# Revit family: 0030453
name_source: partatom
category: Lighting Fixtures
revit_build: Autodesk Revit 2017 (Build: 20190507_1515(x64)
units: mm (PartAtom-declared; Revit-internal decimal feet)

## family parameters
Cut with Voids When Loaded = No
Host = Face
Light Source = Yes
OmniClass Number = 23.80.70.00
OmniClass Title = Lighting
Part Type = Normal
Room Calculation Point = No
Round Connector Dimension = Use Diameter
Shared = No

## types (8) — shared parameters
Apparent Load = 17 VA
Assembly Code = D5020200
AssetType = Fixed
ClassificationName = Uniclass2015
ClassificationValue = EF_70_80
Color Filter = 16777215
Default Elevation = 1219 mm
DiameterRecess_SYL = 200 mm  [stored 0.656168 ft]
DiameterTopBase_SYL = 200 mm  [stored 0.656168 ft]
DiameterTop_SYL = 135 mm  [stored 0.442913 ft]
Diameter_SYL = 220 mm  [stored 0.721785 ft]
Dimming Lamp Color Temperature Shift = <None>
DocumentationLiterature = http://www.sylvania-lighting.com
DurationUnit = hours
ElectricShockClassification = Class II
Emit Shape Visible in Rendering = No
Emit from Circle Diameter = 180 mm  [stored 0.590551 ft]
ExpectedLife = 50000
HeightBezel_SYL = 3 mm  [stored 0.00984252 ft]
Height_SYL = 61 mm  [stored 0.200131 ft]
IfcExportAs = IfcLightFixtureType
IfcExportType = IfcLightFixtureType
ImpactProtectionIndex = IK07
IngressProtection = IP44/20
Keynote = 16500
Lamp = LED
LampColourRenderingIndex = 80
LampColourTemperature = 4000 K
LampMacAdamStep = 3
LampNominalLuminous = 2000 lm
LampsType = LED
LuminousEfficacy = 121 lm/W
Manufacturer = Feilo Sylvania
ManufacturerName = Feilo Sylvania
Material = aluminium housing
Material_1_FEILO = Trim-Sylvania-STARTDownlight-White
Material_2_FEILO = Diffuser-Sylvania-STARTDownlight
Material_3_FEILO = Top-Sylvania-STARTDownlight
Material_4_FEILO = LED-Sylvania-STARTDownlight
Model = Insaver Slim IP44 Multipower U19 205 650-2000lm840
ModelNumber = 0030453
ModelReference = Insaver Slim IP44 Multipower U19 205 650-2000lm840
Name = Insaver Slim IP44 Multipower U19 205 650-2000lm840
NominalDepth = 220 mm  [stored 0.721785 ft]
NominalHeight = 60 mm  [stored 0.19685 ft]
NominalLength = 220 mm  [stored 0.721785 ft]
PowerConsumption = 16.5 W
PowerFactor = 0.9
RadiusReflector_SYL = 100 mm  [stored 0.328084 ft]
RadiusTop_SYL = 6 mm  [stored 0.019685 ft]
Size1_SYL = No
Size2_SYL = No
Size3PIR_SYL = No
Size4_SYL = Yes
Tilt Angle = -90.00°
Type Image = <None>
TypeName = Insaver Slim IP44 Multipower U19 205 650-2000lm840
URL = http://www.sylvania-lighting.com
VisibilityPIR_SYL = No
Voltage = 0 V
Weight = 8.76 kg
WidthBezel_SYL = 20 mm  [stored 0.0656168 ft]
zero-valued in all types: Cost

## per-type parameters (varying)
| type | Photometric Web File |
| 0030453 INSAVER SLIM IP44M U19 205 650-2000LM840_5W | 0030453_5W.ies |
| 0030453 INSAVER SLIM IP44M U19 205 650-2000LM840_6W | 0030453_6W.ies |
| 0030453 INSAVER SLIM IP44M U19 205 650-2000LM840_8W | 0030453_8W.ies |
| 0030453 INSAVER SLIM IP44M U19 205 650-2000LM840_10W | 0030453_10W.ies |
| 0030453 INSAVER SLIM IP44M U19 205 650-2000LM840_11W | 0030453_11W.ies |
| 0030453 INSAVER SLIM IP44M U19 205 650-2000LM840_13W | 0030453_13W.ies |
| 0030453 INSAVER SLIM IP44M U19 205 650-2000LM840_15W | 0030453_15W.ies |
| 0030453 INSAVER SLIM IP44M U19 205 650-2000LM840_16W | 0030453_16W.ies |

note: [stored X ft] marks values corroborated as IEEE doubles in the binary element streams (Revit-internal decimal feet)

## geometry (parser evidence)
native form markers: Sweep x3
no freeform markers — native parametric forms only
